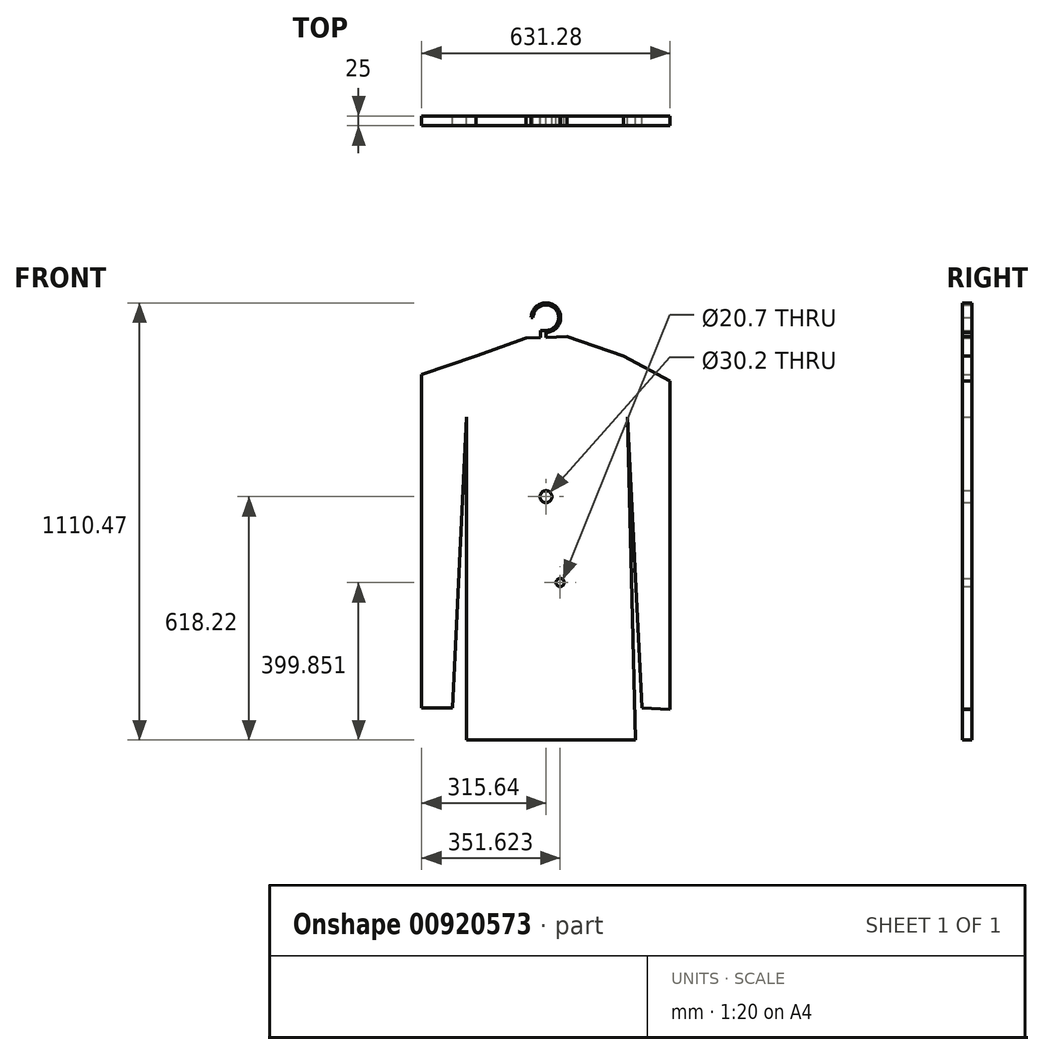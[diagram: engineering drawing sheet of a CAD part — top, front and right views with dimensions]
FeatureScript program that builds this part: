
annotation { "Feature Type Name" : "Feature", "Feature Type Description" : "" }
export const myFeature = defineFeature(function(context is Context, id is Id, definition is map)
    precondition{}
    {
        {
            var Q0;
            Q0=qCreatedBy(makeId("Front.planeOp"),FACE);
            var sketch = newSketch(context, id + "F0", { "sketchPlane" : qUnion([Q0])});
            skPoint(sketch, "E0.middle", {"position": v(0, 0) * mm});
            skLineSegment(sketch, "E1", {"start": v(-315.64, -445.16) * mm, "end": v(-237.92, -445.16) * mm});
            skLineSegment(sketch, "E2", {"start": v(-237.92, -445.16) * mm, "end": v(-202.43, 294.52) * mm});
            skLineSegment(sketch, "E3", {"start": v(-202.43, 294.52) * mm, "end": v(-202.43, -526.06) * mm});
            skLineSegment(sketch, "E4", {"start": v(-202.43, -526.06) * mm, "end": v(227.19, -526.06) * mm});
            skLineSegment(sketch, "E5", {"start": v(227.19, -526.06) * mm, "end": v(206.64, 294.52) * mm});
            skLineSegment(sketch, "E6", {"start": v(206.64, 294.52) * mm, "end": v(244, -445.16) * mm});
            skLineSegment(sketch, "E7", {"start": v(244, -445.16) * mm, "end": v(315.64, -448.6) * mm});
            skLineSegment(sketch, "E8", {"start": v(315.64, -448.6) * mm, "end": v(315.64, 386.05) * mm});
            skLineSegment(sketch, "E9", {"start": v(315.64, 386.05) * mm, "end": v(197.3, 449.55) * mm});
            skLineSegment(sketch, "E10", {"start": v(197.3, 449.55) * mm, "end": v(53.17, 498.22) * mm});
            skLineSegment(sketch, "E11", {"start": v(53.17, 498.22) * mm, "end": v(-50.88, 495.62) * mm});
            skLineSegment(sketch, "E12", {"start": v(-50.88, 495.62) * mm, "end": v(-178.15, 449.55) * mm});
            skLineSegment(sketch, "E13", {"start": v(-178.15, 449.55) * mm, "end": v(-315.64, 402.86) * mm});
            skLineSegment(sketch, "E14", {"start": v(-315.64, 402.86) * mm, "end": v(-315.64, -445.16) * mm});
            skArc(sketch, "E15", {"start": v(0, 514.4) * mm, "mid": v(23.04, 569.83) * mm, "end": v(-32.5, 547.08) * mm});
            skArc(sketch, "E16", {"start": v(0, 509.4) * mm, "mid": v(26.59, 573.35) * mm, "end": v(-37.5, 547.1) * mm});
            skLineSegment(sketch, "E17", {"start": v(-37.5, 547.1) * mm, "end": v(-32.5, 547.08) * mm});
            skPoint(sketch, "E18.orphan", {"position": v(0, 514.62) * mm});
            skLineSegment(sketch, "E19.bottom", {"start": v(0, 514.4) * mm, "end": v(-14.41, 514.4) * mm});
            skLineSegment(sketch, "E19.left", {"start": v(0, 509.4) * mm, "end": v(0, 496.9) * mm});
            skLineSegment(sketch, "E19.right", {"start": v(-14.41, 514.4) * mm, "end": v(-14.41, 496.53) * mm});
            skCircle(sketch, "E20", {"center": v(0, 92.16) * mm, "radius": 15.1 * mm});
            skCircle(sketch, "E21", {"center": v(35.98, -126.2) * mm, "radius": 10.35 * mm});
            skSolve(sketch);
        }
        {
            var Q0;
            Q0 = qSketchRegion(id + "F0", true);
            extrude(context, id + "F1", {"entities" : qUnion([Q0]), "depth" : 25 * mm, "offsetDistance" : 25 * mm, "symmetric" : true});
        }
    });
